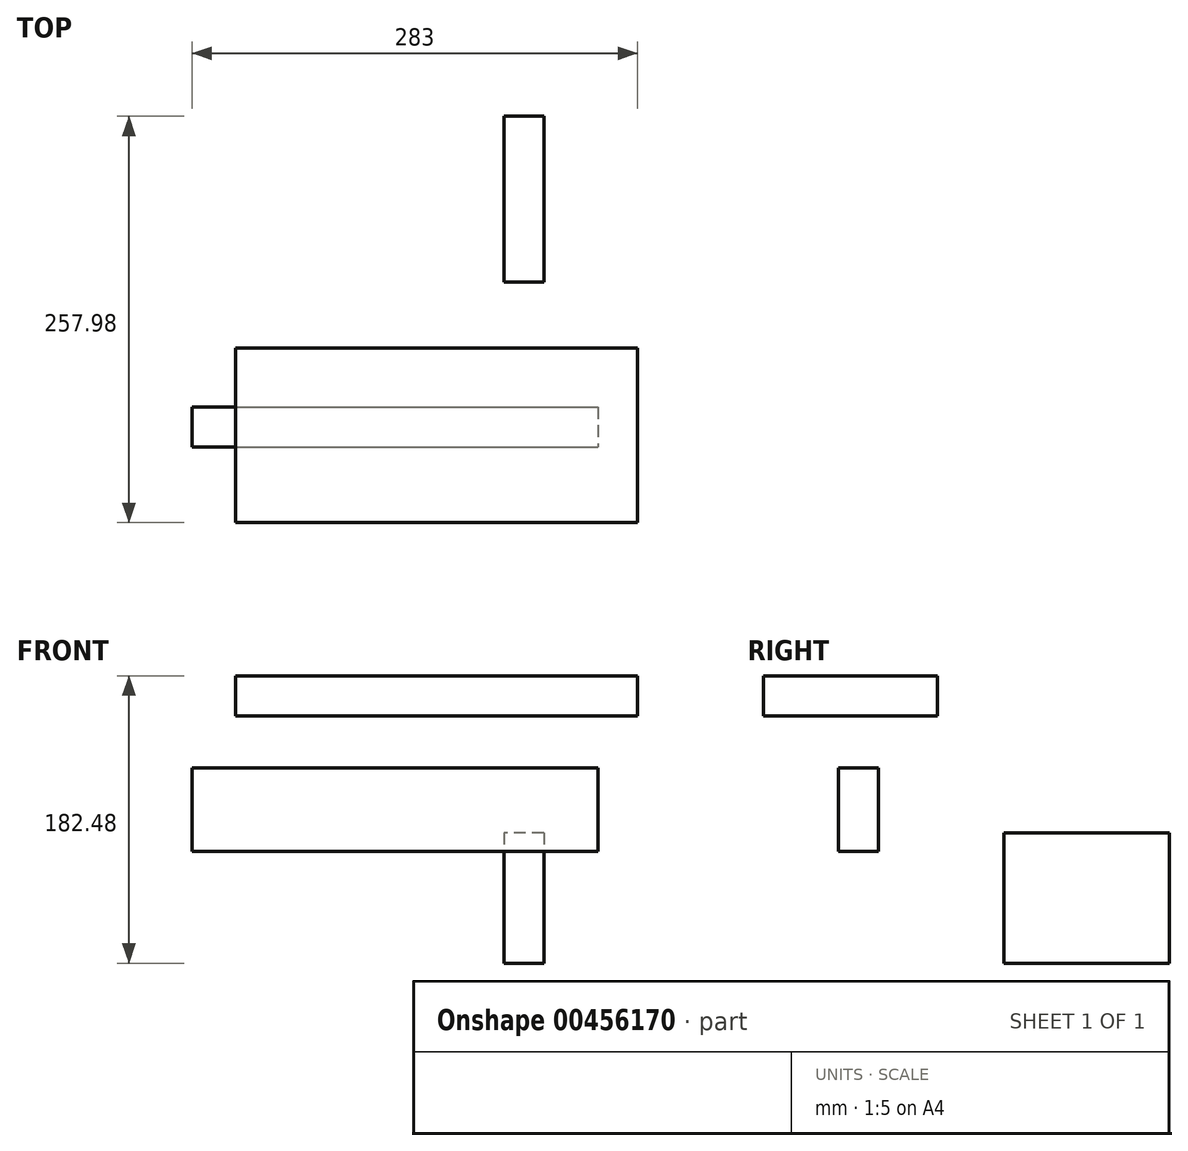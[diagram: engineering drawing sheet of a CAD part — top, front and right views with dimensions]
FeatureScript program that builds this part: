
annotation { "Feature Type Name" : "Feature", "Feature Type Description" : "" }
export const myFeature = defineFeature(function(context is Context, id is Id, definition is map)
    precondition{}
    {
        {
            var Q0;
            Q0=qCreatedBy(makeId("Top.planeOp"),FACE);
            var sketch = newSketch(context, id + "F0", { "sketchPlane" : qUnion([Q0])});
            skLineSegment(sketch, "E0.bottom", {"start": v(-170.25, 62.8) * mm, "end": v(84.89, 62.8) * mm});
            skLineSegment(sketch, "E0.top", {"start": v(-170.25, -22.42) * mm, "end": v(84.89, -22.42) * mm});
            skLineSegment(sketch, "E0.left", {"start": v(-170.25, 62.8) * mm, "end": v(-170.25, -22.42) * mm});
            skLineSegment(sketch, "E0.right", {"start": v(84.89, 62.8) * mm, "end": v(84.89, -22.42) * mm});
            skSolve(sketch);
        }
        {
            var Q0;
            Q0 = qSketchRegion(id + "F0", true);
            extrude(context, id + "F1", {"entities" : qUnion([Q0]), "depth" : 25.4 * mm});
        }
        {
            var Q0;
            Q0=makeQuery(id+"F1.opExtrude","SWEPT_FACE",FACE,{"disambiguationData":[OSD([sQuery(id+"F0.wireOp",EDGE,"E0.top")])]});
            extrude(context, id + "F2", {"entities" : qUnion([Q0]), "operationType" : NewBodyOperationType.ADD, "depth" : 25.4 * mm});
        }
        {
            var Q0;
            Q0=qCreatedBy(makeId("Front.planeOp"),FACE);
            var sketch = newSketch(context, id + "F3", { "sketchPlane" : qUnion([Q0])});
            skLineSegment(sketch, "E1.bottom", {"start": v(-198.11, -32.95) * mm, "end": v(59.96, -32.95) * mm});
            skLineSegment(sketch, "E1.top", {"start": v(-198.11, -86.18) * mm, "end": v(59.96, -86.18) * mm});
            skLineSegment(sketch, "E1.left", {"start": v(-198.11, -32.95) * mm, "end": v(-198.11, -86.18) * mm});
            skLineSegment(sketch, "E1.right", {"start": v(59.96, -32.95) * mm, "end": v(59.96, -86.18) * mm});
            skSolve(sketch);
        }
        {
            var Q0;
            Q0=makeQuery(id+"F3.imprint","IMPRINT",FACE,{"disambiguationData":[TD([[makeQuery(id+"F3.imprint","IMPRINT",EDGE,{"derivedFrom":sQuery(id+"F3.wireOp",EDGE,"E1.bottom")}),-1.0]])]});
            extrude(context, id + "F4", {"entities" : qUnion([Q0]), "oppositeDirection" : true, "depth" : 25.4 * mm});
        }
        {
            var Q0;
            Q0=qCreatedBy(makeId("Right.planeOp"),FACE);
            var sketch = newSketch(context, id + "F5", { "sketchPlane" : qUnion([Q0])});
            skLineSegment(sketch, "E2.bottom", {"start": v(210.16, -74.14) * mm, "end": v(104.9, -74.14) * mm});
            skLineSegment(sketch, "E2.top", {"start": v(210.16, -157.08) * mm, "end": v(104.9, -157.08) * mm});
            skLineSegment(sketch, "E2.left", {"start": v(210.16, -74.14) * mm, "end": v(210.16, -157.08) * mm});
            skLineSegment(sketch, "E2.right", {"start": v(104.9, -74.14) * mm, "end": v(104.9, -157.08) * mm});
            skSolve(sketch);
        }
        {
            var Q0;
            Q0 = qSketchRegion(id + "F5", true);
            extrude(context, id + "F6", {"entities" : qUnion([Q0]), "depth" : 25.4 * mm});
        }
    });
